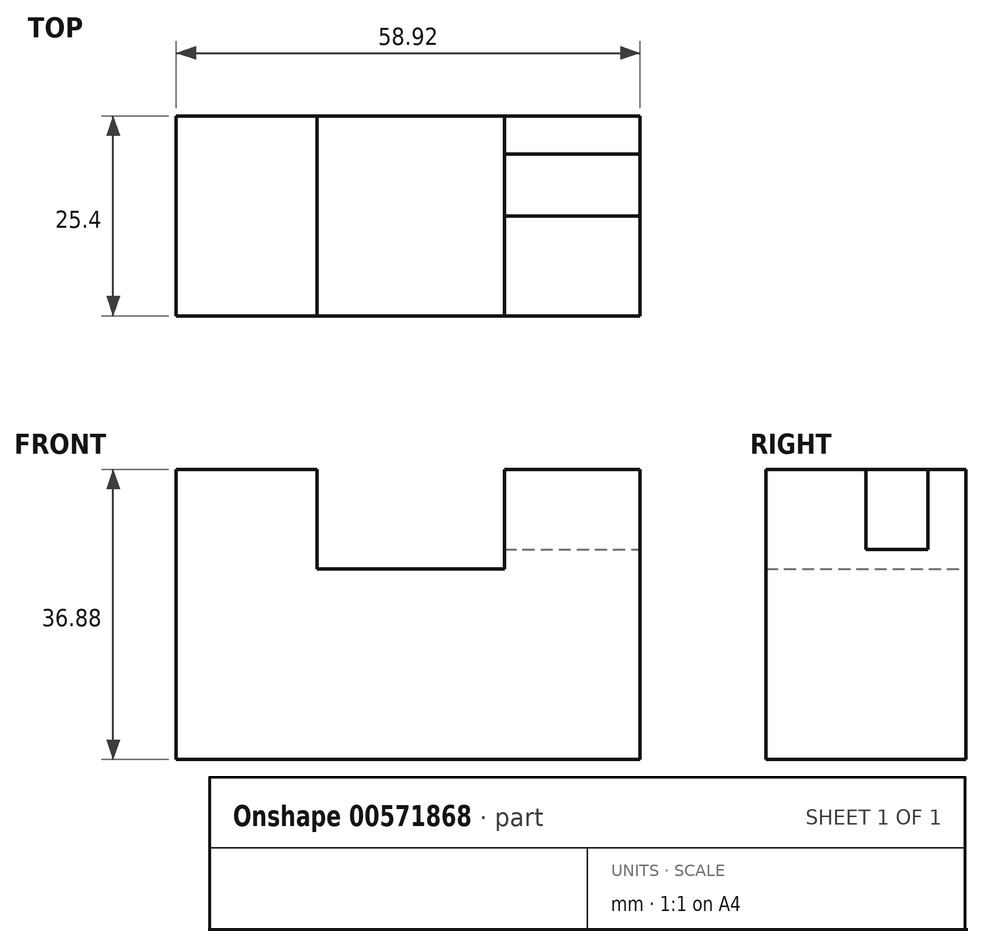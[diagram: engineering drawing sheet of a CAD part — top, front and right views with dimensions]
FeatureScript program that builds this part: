
annotation { "Feature Type Name" : "Feature", "Feature Type Description" : "" }
export const myFeature = defineFeature(function(context is Context, id is Id, definition is map)
    precondition{}
    {
        {
            var Q0;
            Q0=qCreatedBy(makeId("Front.planeOp"),FACE);
            var sketch = newSketch(context, id + "F0", { "sketchPlane" : qUnion([Q0])});
            skLineSegment(sketch, "E0.bottom", {"start": v(0, 0) * mm, "end": v(58.92, 0) * mm});
            skLineSegment(sketch, "E0.top", {"start": v(0, 36.88) * mm, "end": v(17.87, 36.88) * mm});
            skLineSegment(sketch, "E0.left", {"start": v(0, 0) * mm, "end": v(0, 36.88) * mm});
            skLineSegment(sketch, "E0.right", {"start": v(58.92, 0) * mm, "end": v(58.92, 36.88) * mm});
            skLineSegment(sketch, "E1.top", {"start": v(17.87, 24.21) * mm, "end": v(41.7, 24.21) * mm});
            skLineSegment(sketch, "E1.left", {"start": v(17.87, 36.88) * mm, "end": v(17.87, 24.21) * mm});
            skLineSegment(sketch, "E1.right", {"start": v(41.7, 36.88) * mm, "end": v(41.7, 24.21) * mm});
            skLineSegment(sketch, "E2.trimOffspring", {"start": v(41.7, 36.88) * mm, "end": v(58.92, 36.88) * mm});
            skSolve(sketch);
        }
        {
            var Q0;
            Q0=makeQuery(id+"F0.imprint","IMPRINT",FACE,{"disambiguationData":[TD([[makeQuery(id+"F0.imprint","IMPRINT",EDGE,{"derivedFrom":sQuery(id+"F0.wireOp",EDGE,"E0.bottom")}),1.0]])]});
            extrude(context, id + "F1", {"entities" : qUnion([Q0]), "depth" : 25.4 * mm, "offsetDistance" : 25.4 * mm});
        }
        {
            var Q0;
            Q0=makeQuery(id+"F1.opExtrude","SWEPT_FACE",FACE,{"disambiguationData":[OSD([sQuery(id+"F0.wireOp",EDGE,"E2.trimOffspring")])]});
            var sketch = newSketch(context, id + "F2", { "sketchPlane" : qUnion([Q0])});
            skLineSegment(sketch, "E3.bottom", {"start": v(41.7, -12.7) * mm, "end": v(58.92, -12.7) * mm});
            skLineSegment(sketch, "E3.top", {"start": v(41.7, -4.83) * mm, "end": v(58.92, -4.83) * mm});
            skLineSegment(sketch, "E3.left", {"start": v(41.7, -12.7) * mm, "end": v(41.7, -4.83) * mm});
            skLineSegment(sketch, "E3.right", {"start": v(58.92, -12.7) * mm, "end": v(58.92, -4.83) * mm});
            skSolve(sketch);
        }
        {
            var Q0;
            Q0 = qSketchRegion(id + "F2", true);
            extrude(context, id + "F3", {"entities" : qUnion([Q0]), "operationType" : NewBodyOperationType.REMOVE, "oppositeDirection" : true, "depth" : 10.16 * mm, "offsetDistance" : 25.4 * mm});
        }
    });
